# Revit family: Shower-Handshower_Kit-KOHLER-Urbanity-K-23748T_1
name_source: partatom
category: Plumbing Fixtures
units: mm (PartAtom-declared; Revit-internal decimal feet)

## family parameters
Cut with Voids When Loaded = No
Host = Face
OmniClass Number = 23.31.17.00
OmniClass Title = Showers
Part Type = Normal
Room Calculation Point = No
Round Connector Dimension = Use Diameter
Shared = No

## types (5) — shared parameters
ADA Compliant = No
Assembly Code = D2010700
CW Connection = Yes
Cold Water Inlet = Cold Water Inlet
Date Modified = 11/16/2022
Default Elevation = 42"
Description = Lingkin Wall-Mounted Bathtub Shower Faucet
Drain Included = No
Flow Rate = 3 GPM
HW Connection = Yes
Height = 2 15/16"
Hot Water Inlet = Hot Water Inlet
Length = 6"
Manufacturer = Kohler Co.
Master Format 2014 = 22 42 23
Master Format 2014 Name = Residential Showers
Material = Premium Metal Construction
Panel Thickness = 4 15/16"
Pressure = 60.00 psi
Product Documentation Link = https://files.kohler.com.cn
Product Name = Urbanity
URL = http://www.kohler.com.cn
Vent Connection = No
Waste Connection = No
Waste Water Outlet = Waste Water Outlet
WaterSense Certified = No
Width = 11 7/16"

## per-type parameters (varying)
| type | Back Plate | Face Plate Finish | Finish | Model | Product Page URL | Secondary Finish | Type |
| CP-Polished Chrome | Kohler-Plastic-0-White | Kohler-Plastic-0-White | Kohler-Metal-CP-Polished_Chrome | K-23748T-9-CP | https://www.kohler.com.cn | Kohler-Plastic-0-White | 1 |
| CY-Thunder Grey | Kohler-Plastic-BL-Matte_Black | Kohler-Plastic-0-White | Kohler-Metal-CP-Polished_Chrome | K-23748T-9-CY | https://www.kohler.com.cn | Kohler-Plastic-58-Thunder_Grey | 2 |
| BL-Matte Black | Kohler-Plastic-58-Thunder_Grey | Kohler-Plastic-BL-Matte_Black | Kohler-Metal-BL-Matte_Black | K-23748T-9-BL | https://www.kohler.com.cn | Kohler-Plastic-BL-Matte_Black | 3 |
| 2MB-Vibrant Brushed Moderne Brass | Kohler-Plastic-58-Thunder_Grey | Kohler-Plastic-BL-Matte_Black | Kohler-Metal-2MB-Vibrant_Brushed_Moderne_Brass | K-23748T-9-2MB | https://www.kohler.com.cn | Kohler-Plastic-BL-Matte_Black | 4 |
| RGD-Polished Rose Gold | Kohler-Plastic-0-White | Kohler-Plastic-0-White | Kohler-Metal-RGD-Polished_Rose_Gold | K-23748T-9-RGD |  | Kohler-Plastic-0-White | 5 |

## geometry (parser evidence)
native form markers: Sweep x5
no freeform markers — native parametric forms only
